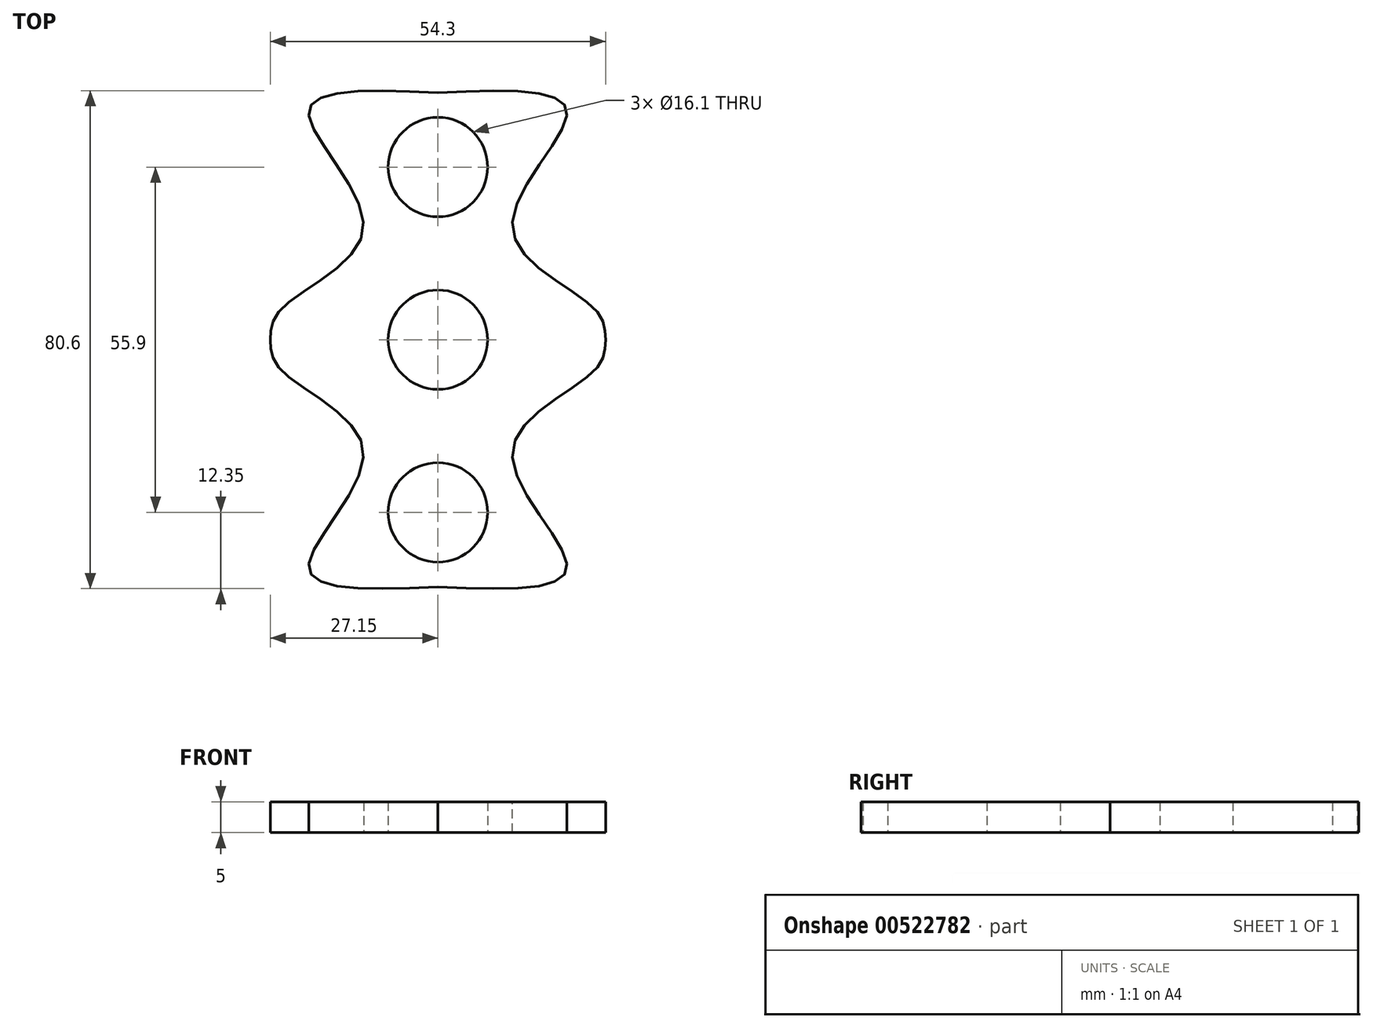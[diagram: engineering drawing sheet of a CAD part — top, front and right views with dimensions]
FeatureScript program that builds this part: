
annotation { "Feature Type Name" : "Feature", "Feature Type Description" : "" }
export const myFeature = defineFeature(function(context is Context, id is Id, definition is map)
    precondition{}
    {
        {
            var Q0;
            Q0=qCreatedBy(makeId("Top.planeOp"),FACE);
            var sketch = newSketch(context, id + "F0", { "sketchPlane" : qUnion([Q0])});
            skCircle(sketch, "E0", {"center": v(0, 0) * mm, "radius": 8.05 * mm});
            skCircle(sketch, "E1", {"center": v(0, 27.95) * mm, "radius": 8.05 * mm});
            skCircle(sketch, "E2", {"center": v(0, 0) * mm, "radius": 40 * mm, "construction": true});
            skCircle(sketch, "E3.0", {"center": v(0, 0) * mm, "radius": 16.05 * mm});
            skCircle(sketch, "E4.0", {"center": v(0, 27.95) * mm, "radius": 12.05 * mm, "construction": true});
            skLineSegment(sketch, "E5", {"start": v(0, 0) * mm, "end": v(0, 55.77) * mm, "construction": true});
            skFitSpline(sketch, "E6", {"points": [v(0, 40) * mm, v(-20.9, 36.86) * mm, v(-12.06, 18.13) * mm, v(-25.24, 5.12) * mm, v(-27.15, 0) * mm], "startDerivative": vector(-106.27, 4.83) * mm, "endDerivative": vector(-0.86, -33.58) * mm});
            skFitSpline(sketch, "E7.MirrorCS", {"points": [v(0, 40) * mm, v(20.9, 36.86) * mm, v(12.06, 18.13) * mm, v(25.24, 5.12) * mm, v(27.15, 0) * mm], "startDerivative": vector(106.27, 4.83) * mm, "endDerivative": vector(0.86, -33.58) * mm});
            skPoint(sketch, "E8.orphan", {"position": v(-33.91, 0) * mm});
            skLineSegment(sketch, "E9", {"start": v(-33.91, 0) * mm, "end": v(34.95, 0) * mm, "construction": true});
            skFitSpline(sketch, "E10.MirrorCS", {"points": [v(0, -40) * mm, v(-20.9, -36.86) * mm, v(-12.06, -18.13) * mm, v(-25.24, -5.12) * mm, v(-27.15, 0) * mm], "startDerivative": vector(-106.27, -4.83) * mm, "endDerivative": vector(-0.86, 33.58) * mm});
            skFitSpline(sketch, "E11.MirrorCS", {"points": [v(0, -40) * mm, v(20.9, -36.86) * mm, v(12.06, -18.13) * mm, v(25.24, -5.12) * mm, v(27.15, 0) * mm], "startDerivative": vector(106.27, -4.83) * mm, "endDerivative": vector(0.86, 33.58) * mm});
            skCircle(sketch, "E12.MirrorC", {"center": v(0, -27.95) * mm, "radius": 8.05 * mm});
            skSolve(sketch);
        }
        {
            var Q0;
            Q0=makeQuery(id+"F0.imprint","IMPRINT",FACE,{"disambiguationData":[TD([[makeQuery(id+"F0.imprint","IMPRINT",EDGE,{"derivedFrom":sQuery(id+"F0.wireOp",EDGE,"E0")}),-1.0]])]});
            extrude(context, id + "F1", {"entities" : qUnion([Q0]), "depth" : 5 * mm, "offsetDistance" : 25 * mm});
        }
        {
            var Q0;
            Q0=makeQuery(id+"F0.imprint","IMPRINT",FACE,{"disambiguationData":[TD([[makeQuery(id+"F0.imprint","IMPRINT",EDGE,{"derivedFrom":sQuery(id+"F0.wireOp",EDGE,"E1")}),-1.0]])]});
            extrude(context, id + "F2", {"entities" : qUnion([Q0]), "operationType" : NewBodyOperationType.ADD, "depth" : 5 * mm, "offsetDistance" : 25 * mm});
        }
    });
